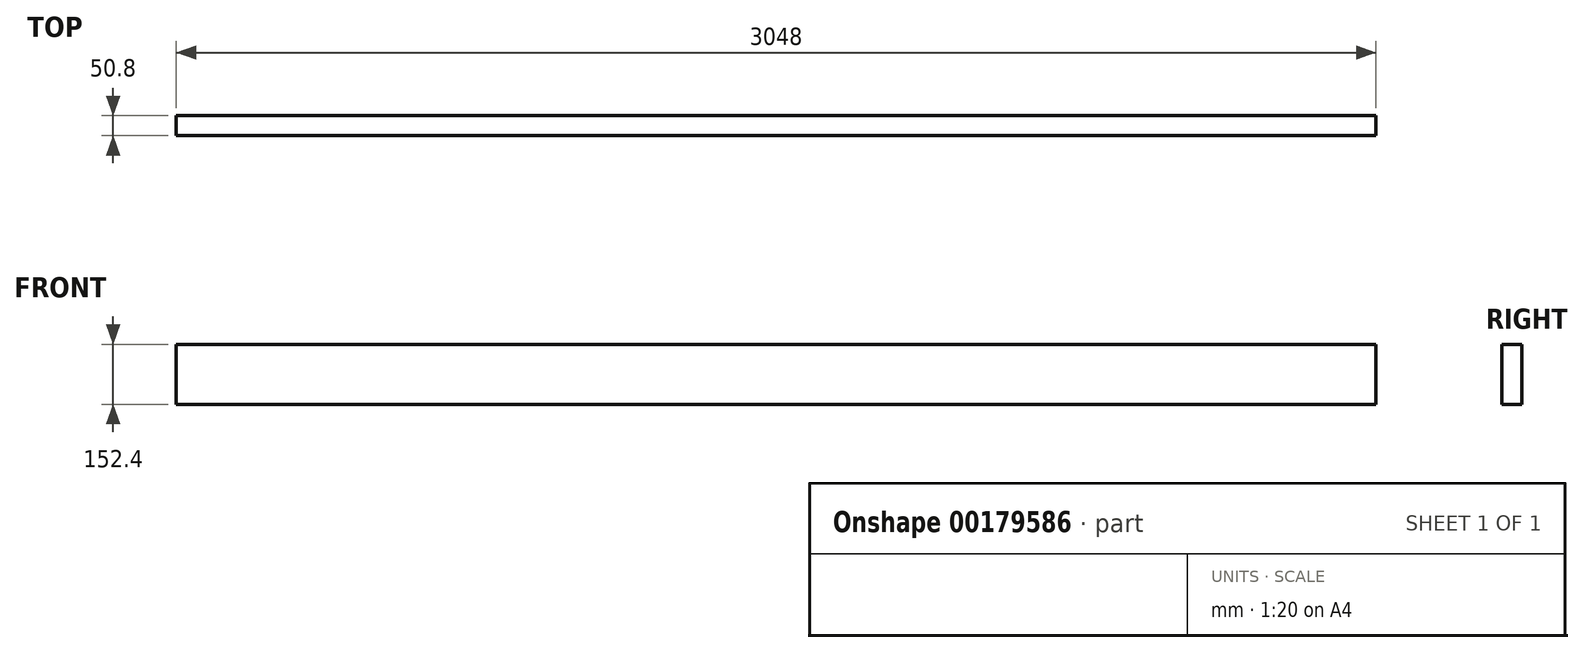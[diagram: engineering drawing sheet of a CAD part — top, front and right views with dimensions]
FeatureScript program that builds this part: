
annotation { "Feature Type Name" : "Feature", "Feature Type Description" : "" }
export const myFeature = defineFeature(function(context is Context, id is Id, definition is map)
    precondition{}
    {
        {
            var Q0;
            Q0=qCreatedBy(makeId("Top.planeOp"),FACE);
            var sketch = newSketch(context, id + "F0", { "sketchPlane" : qUnion([Q0])});
            skLineSegment(sketch, "E0.bottom", {"start": v(-1524, 25.4) * mm, "end": v(1524, 25.4) * mm});
            skLineSegment(sketch, "E0.top", {"start": v(-1524, -25.4) * mm, "end": v(1524, -25.4) * mm});
            skLineSegment(sketch, "E0.left", {"start": v(-1524, 25.4) * mm, "end": v(-1524, -25.4) * mm});
            skLineSegment(sketch, "E0.right", {"start": v(1524, 25.4) * mm, "end": v(1524, -25.4) * mm});
            skPoint(sketch, "E0.middle", {"position": v(0, 0) * mm});
            skSolve(sketch);
        }
        {
            var Q0;
            Q0 = qSketchRegion(id + "F0", true);
            extrude(context, id + "F1", {"entities" : qUnion([Q0]), "depth" : 152.4 * mm});
        }
    });
